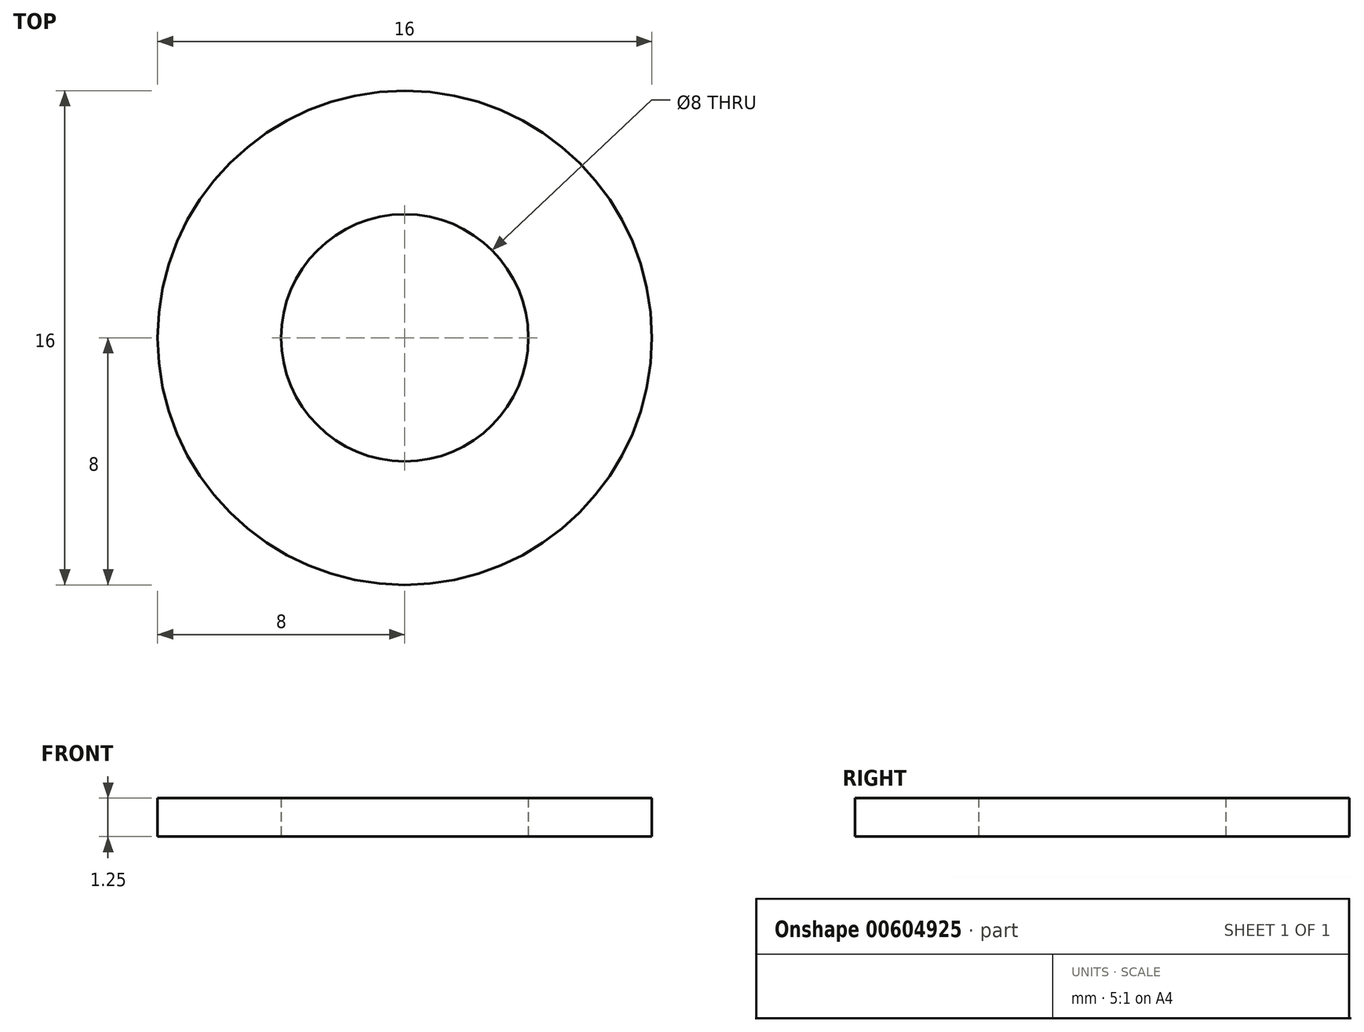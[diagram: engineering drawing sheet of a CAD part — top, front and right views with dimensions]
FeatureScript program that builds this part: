
annotation { "Feature Type Name" : "Feature", "Feature Type Description" : "" }
export const myFeature = defineFeature(function(context is Context, id is Id, definition is map)
    precondition{}
    {
        {
            var Q0;
            Q0=qCreatedBy(makeId("Top.planeOp"),FACE);
            var sketch = newSketch(context, id + "F0", { "sketchPlane" : qUnion([Q0])});
            skCircle(sketch, "E0", {"center": v(0, 0) * mm, "radius": 4 * mm});
            skCircle(sketch, "E1", {"center": v(0, 0) * mm, "radius": 8 * mm});
            skSolve(sketch);
        }
        {
            var Q0;
            Q0 = qSketchRegion(id + "F0", true);
            extrude(context, id + "F1", {"entities" : qUnion([Q0]), "depth" : 1.25 * mm, "offsetDistance" : 25 * mm});
        }
    });
